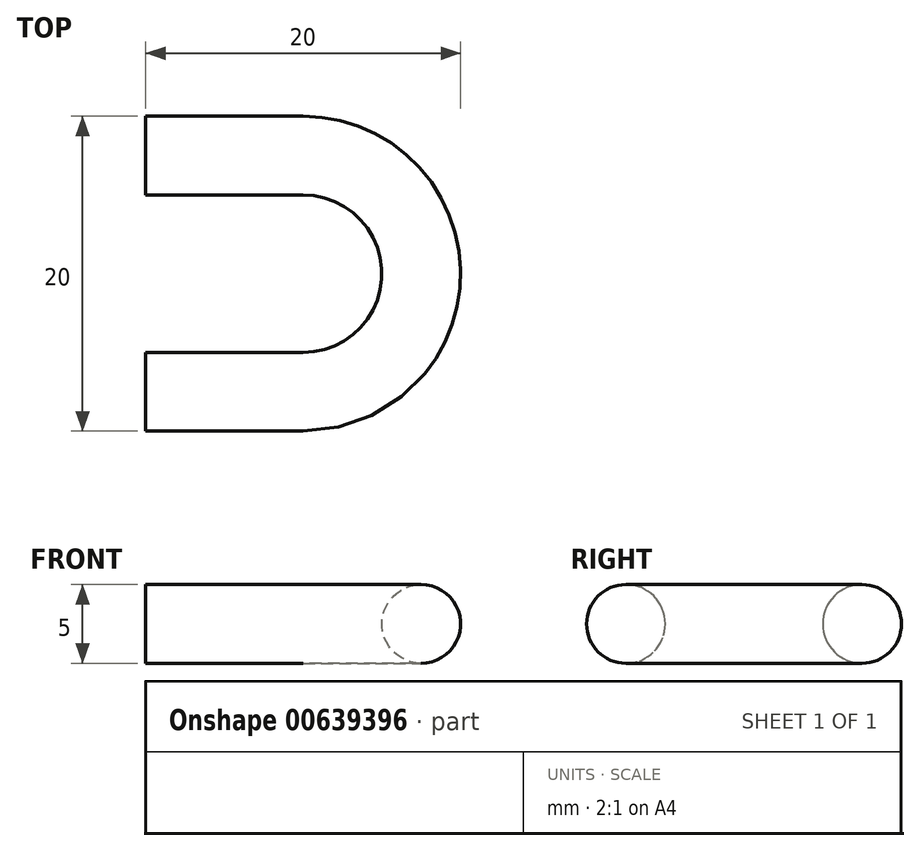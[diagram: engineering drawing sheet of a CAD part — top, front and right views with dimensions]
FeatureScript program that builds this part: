
annotation { "Feature Type Name" : "Feature", "Feature Type Description" : "" }
export const myFeature = defineFeature(function(context is Context, id is Id, definition is map)
    precondition{}
    {
        {
            var Q0;
            Q0=qCreatedBy(makeId("Top.planeOp"),FACE);
            var sketch = newSketch(context, id + "F0", { "sketchPlane" : qUnion([Q0])});
            skLineSegment(sketch, "E0", {"start": v(0, 0) * mm, "end": v(10, 0) * mm});
            skLineSegment(sketch, "E1", {"start": v(0, 15) * mm, "end": v(10, 15) * mm});
            skArc(sketch, "E2", {"start": v(10, 0) * mm, "mid": v(17.5, 7.5) * mm, "end": v(10, 15) * mm});
            skSolve(sketch);
        }
        {
            var Q0;
            Q0=qCreatedBy(makeId("Right.planeOp"),FACE);
            var sketch = newSketch(context, id + "F1", { "sketchPlane" : qUnion([Q0])});
            skCircle(sketch, "E3", {"center": v(0, 0) * mm, "radius": 2.5 * mm});
            skSolve(sketch);
        }
        {
            var Q0;
            Q0=makeQuery(id+"F1.imprint","IMPRINT",FACE,{"disambiguationData":[TD([[makeQuery(id+"F1.imprint","IMPRINT",EDGE,{"derivedFrom":sQuery(id+"F1.wireOp",EDGE,"E3")}),1.0]])]});
            var Q1;
            Q1=sQuery(id+"F0.wireOp",EDGE,"E0");
            var Q2;
            Q2=sQuery(id+"F0.wireOp",EDGE,"E2");
            var Q3;
            Q3=sQuery(id+"F0.wireOp",EDGE,"E1");
            sweep(context, id + "F2", {"profiles" : qUnion([Q0]), "path" : qUnion([Q1, Q2, Q3])});
        }
    });
